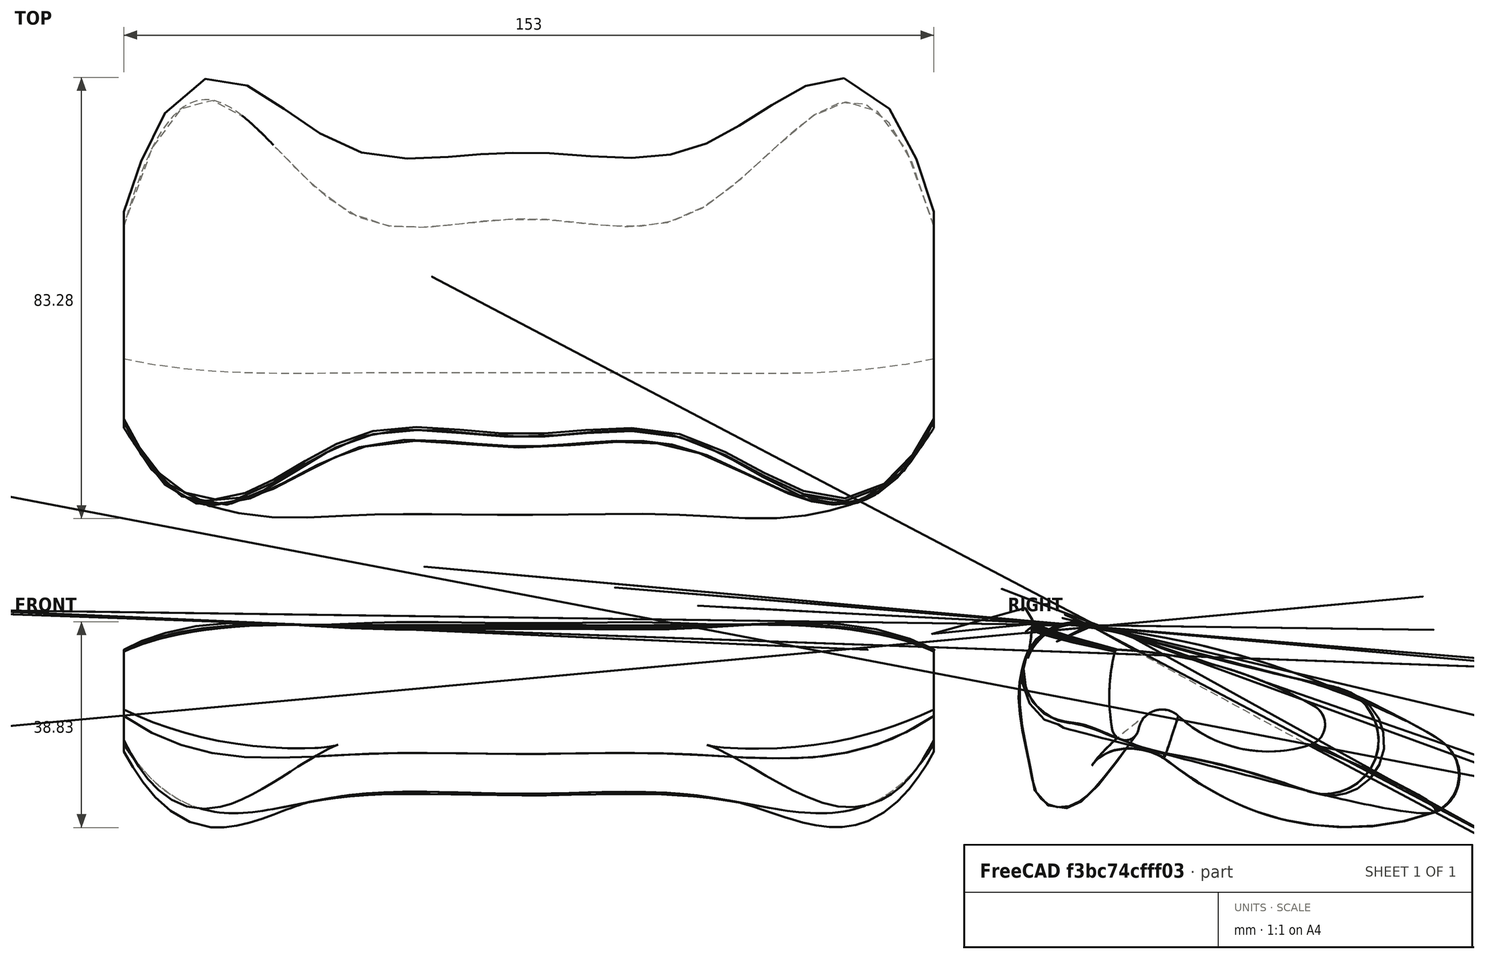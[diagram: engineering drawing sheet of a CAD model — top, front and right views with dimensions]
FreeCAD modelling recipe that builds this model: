
FCSTD DOCUMENT  (FreeCAD 0.20R29410 (Git))
Label: manette
License: All rights reserved
LicenseURL: http://en.wikipedia.org/wiki/All_rights_reserved
objects: Part::FeaturePython×9, Sketcher::SketchObject×7, Part::Face×2
note: 18 computed .brp shape members not serialized (recipe doc carries the construction recipe); baked Part::Feature solids carry a one-line shape summary decoded from their .brp

FEATURE [Sketcher::SketchObject] Sketch001
  FullyConstrained = true
  Placement = pos=(0,0,0) rot=(0.57735,0.57735,0.57735;2.0944rad)
  sketch-geometry (7):
    g0: ArcOfCircle CenterX=51.2288 CenterY=20.8676 CenterZ=0 NormalX=0 NormalY=0 NormalZ=1 AngleXU=0 Radius=4 StartAngle=5.03579 EndAngle=7.33836
    g1: ArcOfCircle CenterX=44.5551 CenterY=40.779 CenterZ=0 NormalX=0 NormalY=0 NormalZ=1 AngleXU=0 Radius=25 StartAngle=3.96161 EndAngle=5.03579
    g2: ArcOfCircle CenterX=24.4301 CenterY=19.2098 CenterZ=0 NormalX=0 NormalY=0 NormalZ=1 AngleXU=0 Radius=4.5 StartAngle=0.820021 EndAngle=2.96507
    g3: ArcOfCircle CenterX=17.5 CenterY=20.4459 CenterZ=0 NormalX=0 NormalY=0 NormalZ=1 AngleXU=0 Radius=2.53946 StartAngle=3.31811 EndAngle=6.10667
    g4: ArcOfCircle CenterX=49.2692 CenterY=26.1128 CenterZ=0 NormalX=0 NormalY=0 NormalZ=1 AngleXU=0 Radius=34.8101 StartAngle=2.89464 EndAngle=3.31811
    g5: ArcOfCircle CenterX=12.5223 CenterY=-47.4262 CenterZ=0 NormalX=0 NormalY=0 NormalZ=1 AngleXU=0 Radius=82.5 StartAngle=1.05517 EndAngle=1.52837
    g6: ArcOfCircle CenterX=16 CenterY=34.5 CenterZ=0 NormalX=0 NormalY=0 NormalZ=1 AngleXU=0 Radius=0.5 StartAngle=1.52837 EndAngle=2.89464
  constraints (21):
    c: Tangent(g2,g3) = 1.5708
    c: Tangent(g2,g1) = 1.5708
    c: Tangent(g1,g0) = -1.5708
    c: Tangent(g3,g4) = -1.5708
    c: Tangent(g0,g5) = -1.5708
    c: DistanceX(g1,g0) = 25
    c: DistanceX(g2,g1) = 7.5
    c: DistanceY(g3,g2) = 0
    c: DistanceX(g3,g2) = 5
    c: DistanceX(g-1,g3) = 15
    c: DistanceY(g-1,g3) = 20
    c: Radius(g1) = 25
    c: Radius(g2) = 4.5
    c: Radius(g0) = 4
    c: Radius(g5) = 82.5
    c: Tangent(g5,g6) = -1.5708
    c: Tangent(g4,g6) = -1.5708
    c: Radius(g6) = 0.5
    c: DistanceX(g3,g6) = 1
    c: DistanceY(g3,g6) = 14.5
    c: DistanceY(g-1,g1) = 22.5
FEATURE [Sketcher::SketchObject] Sketch002
  FullyConstrained = true
  Placement = pos=(20,0,0) rot=(0.57735,0.57735,0.57735;2.0944rad)
  sketch-geometry (7):
    g0: ArcOfCircle CenterX=72.5307 CenterY=11.5172 CenterZ=0 NormalX=0 NormalY=0 NormalZ=1 AngleXU=0 Radius=7.77 StartAngle=5.03579 EndAngle=7.33312
    g1: ArcOfCircle CenterX=59.1103 CenterY=51.558 CenterZ=0 NormalX=0 NormalY=0 NormalZ=1 AngleXU=0 Radius=50 StartAngle=3.96161 EndAngle=5.03579
    g2: ArcOfCircle CenterX=18.8601 CenterY=8.41956 CenterZ=0 NormalX=0 NormalY=0 NormalZ=1 AngleXU=0 Radius=9 StartAngle=0.820021 EndAngle=2.96507
    g3: ArcOfCircle CenterX=5 CenterY=10.8919 CenterZ=0 NormalX=0 NormalY=0 NormalZ=1 AngleXU=0 Radius=5.07892 StartAngle=3.31811 EndAngle=6.10667
    g4: ArcOfCircle CenterX=81.5376 CenterY=24.5444 CenterZ=0 NormalX=0 NormalY=0 NormalZ=1 AngleXU=0 Radius=82.8246 StartAngle=2.96399 EndAngle=3.31811
    g5: ArcOfCircle CenterX=-5.71127 CenterY=-124.863 CenterZ=0 NormalX=0 NormalY=0 NormalZ=1 AngleXU=0 Radius=165 StartAngle=1.04993 EndAngle=1.52986
    g6: ArcOfCircle CenterX=1 CenterY=39 CenterZ=0 NormalX=0 NormalY=0 NormalZ=1 AngleXU=0 Radius=1 StartAngle=1.52986 EndAngle=2.96399
  constraints (21):
    c: Tangent(g2,g3) = 1.5708
    c: Tangent(g2,g1) = 1.5708
    c: Tangent(g1,g0) = -1.5708
    c: Tangent(g3,g4) = -1.5708
    c: DistanceY(g1) = 15
    c: Tangent(g0,g5) = -1.5708
    c: DistanceX(g1,g0) = 50
    c: DistanceX(g2,g1) = 15
    c: DistanceY(g3,g2) = 0
    c: DistanceX(g3,g2) = 10
    c: DistanceX(g-1,g3) = 0
    c: DistanceY(g-1,g3) = 10
    c: Radius(g1) = 50
    c: Radius(g2) = 9
    c: Radius(g0) = 7.77
    c: Radius(g5) = 165
    c: Tangent(g5,g6) = -1.5708
    c: Tangent(g4,g6) = -1.5708
    c: Radius(g6) = 1
    c: DistanceX(g3,g6) = 1
    c: DistanceY(g3,g6) = 29
FEATURE [Sketcher::SketchObject] Sketch  label="Sketch003"
  FullyConstrained = true
  Placement = pos=(45,0,0) rot=(0.57735,0.57735,0.57735;2.0944rad)
  sketch-geometry (7):
    g0: ArcOfCircle CenterX=56.4123 CenterY=17.5 CenterZ=0 NormalX=0 NormalY=0 NormalZ=1 AngleXU=0 Radius=10 StartAngle=4.45971 EndAngle=7.6013
    g1: LineSegment StartX=13.246 StartY=18.3175 StartZ=0 EndX=24.8649 EndY=15.3175 EndZ=0
    g2: LineSegment StartX=24.8649 StartY=15.3175 StartZ=0 EndX=53.9123 EndY=7.81754 EndZ=0
    g3: ArcOfCircle CenterX=8 CenterY=30 CenterZ=0 NormalX=0 NormalY=0 NormalZ=1 AngleXU=0 Radius=10 StartAngle=1.31812 EndAngle=4.45971
    g4: LineSegment StartX=5.5 StartY=20.3175 StartZ=0 EndX=13.246 EndY=18.3175 EndZ=0
    g5: LineSegment StartX=58.9123 StartY=27.1825 StartZ=0 EndX=13.4047 EndY=38.9325 EndZ=0
    g6: LineSegment StartX=13.4047 StartY=38.9325 StartZ=0 EndX=10.5 EndY=39.6825 EndZ=0
  constraints (17):
    c: Tangent(g2,g0) = -1.5708
    c: Tangent(g0,g5) = -1.5708
    c: DistanceY(g-1,g0) = 17.5
    c: Distance(g3,g2) = 50
    c: Distance(g1) = 12
    c: Radius(g0) = 10
    c: Equal(g3,g0)
    c: Tangent(g4,g1) = -1.5708
    c: Tangent(g1,g2) = -1.5708
    c: Tangent(g4,g3) = -1.5708
    c: Tangent(g3,g6) = -1.5708
    c: DistanceX(g-1,g3) = 8
    c: DistanceY(g-1,g3) = 30
    c: Coincident(g5,g6)
    c: Tangent(g5,g6,g5) = -1.5708
    c: Distance(g6) = 3
    c: Distance(g4) = 8
FEATURE [Sketcher::SketchObject] Sketch003  label="Sketch005"
  FullyConstrained = true
  Placement = pos=(105,0,0) rot=(0.57735,0.57735,0.57735;2.0944rad)
  sketch-geometry (7):
    g0: ArcOfCircle CenterX=56.4123 CenterY=17.5 CenterZ=0 NormalX=0 NormalY=0 NormalZ=1 AngleXU=0 Radius=10 StartAngle=4.45971 EndAngle=7.6013
    g1: LineSegment StartX=5.5 StartY=20.3175 StartZ=0 EndX=13.246 EndY=18.3175 EndZ=0
    g2: LineSegment StartX=13.246 StartY=18.3175 StartZ=0 EndX=24.8649 EndY=15.3175 EndZ=0
    g3: LineSegment StartX=24.8649 StartY=15.3175 StartZ=0 EndX=53.9123 EndY=7.81754 EndZ=0
    g4: ArcOfCircle CenterX=8 CenterY=30 CenterZ=0 NormalX=0 NormalY=0 NormalZ=1 AngleXU=0 Radius=10 StartAngle=1.31812 EndAngle=4.45971
    g5: LineSegment StartX=58.9123 StartY=27.1825 StartZ=0 EndX=13.4047 EndY=38.9325 EndZ=0
    g6: LineSegment StartX=13.4047 StartY=38.9325 StartZ=0 EndX=10.5 EndY=39.6825 EndZ=0
  constraints (16):
    c: Tangent(g3,g0) = -1.5708
    c: Tangent(g0,g5) = -1.5708
    c: DistanceY(g-1,g0) = 17.5
    c: Distance(g1,g3) = 50
    c: Distance(g1) = 8
    c: Distance(g2) = 12
    c: Radius(g0) = 10
    c: DistanceY(g-1,g4) = 30
    c: Tangent(g1,g2) = -1.5708
    c: Tangent(g2,g3) = -1.5708
    c: Tangent(g4,g1) = -1.5708
    c: Tangent(g4,g6) = -1.5708
    c: DistanceX(g-1,g4) = 8
    c: Parallel(g5,g3)
    c: Tangent(g5,g6) = -1.5708
    c: Distance(g6) = 3
FEATURE [Sketcher::SketchObject] Sketch004  label="Sketch006"
  FullyConstrained = true
  Placement = pos=(133,0,0) rot=(0.57735,0.57735,0.57735;2.0944rad)
  sketch-geometry (7):
    g0: ArcOfCircle CenterX=72.5307 CenterY=11.5172 CenterZ=0 NormalX=0 NormalY=0 NormalZ=1 AngleXU=0 Radius=7.77 StartAngle=5.03579 EndAngle=7.33312
    g1: ArcOfCircle CenterX=59.1103 CenterY=51.558 CenterZ=0 NormalX=0 NormalY=0 NormalZ=1 AngleXU=0 Radius=50 StartAngle=3.96161 EndAngle=5.03579
    g2: ArcOfCircle CenterX=18.8601 CenterY=8.41956 CenterZ=0 NormalX=0 NormalY=0 NormalZ=1 AngleXU=0 Radius=9 StartAngle=0.820021 EndAngle=2.96507
    g3: ArcOfCircle CenterX=5 CenterY=10.8919 CenterZ=0 NormalX=0 NormalY=0 NormalZ=1 AngleXU=0 Radius=5.07892 StartAngle=3.31811 EndAngle=6.10667
    g4: ArcOfCircle CenterX=81.5376 CenterY=24.5444 CenterZ=0 NormalX=0 NormalY=0 NormalZ=1 AngleXU=0 Radius=82.8246 StartAngle=2.96399 EndAngle=3.31811
    g5: ArcOfCircle CenterX=-5.71127 CenterY=-124.863 CenterZ=0 NormalX=0 NormalY=0 NormalZ=1 AngleXU=0 Radius=165 StartAngle=1.04993 EndAngle=1.52986
    g6: ArcOfCircle CenterX=1 CenterY=39 CenterZ=0 NormalX=0 NormalY=0 NormalZ=1 AngleXU=0 Radius=1 StartAngle=1.52986 EndAngle=2.96399
  constraints (21):
    c: Tangent(g2,g3) = 1.5708
    c: Tangent(g2,g1) = 1.5708
    c: Tangent(g1,g0) = -1.5708
    c: Tangent(g3,g4) = -1.5708
    c: DistanceY(g1) = 15
    c: Tangent(g0,g5) = -1.5708
    c: DistanceX(g1,g0) = 50
    c: DistanceX(g2,g1) = 15
    c: DistanceY(g3,g2) = 0
    c: DistanceX(g3,g2) = 10
    c: DistanceX(g-1,g3) = 0
    c: DistanceY(g-1,g3) = 10
    c: Radius(g1) = 50
    c: Radius(g2) = 9
    c: Radius(g0) = 7.77
    c: Radius(g5) = 165
    c: Tangent(g5,g6) = -1.5708
    c: Tangent(g4,g6) = -1.5708
    c: Radius(g6) = 1
    c: DistanceX(g3,g6) = 1
    c: DistanceY(g3,g6) = 29
FEATURE [Sketcher::SketchObject] Sketch005  label="Sketch007"
  FullyConstrained = true
  Placement = pos=(153,0,0) rot=(0.57735,0.57735,0.57735;2.0944rad)
  sketch-geometry (7):
    g0: ArcOfCircle CenterX=51.2288 CenterY=20.8676 CenterZ=0 NormalX=0 NormalY=0 NormalZ=1 AngleXU=0 Radius=4 StartAngle=5.03579 EndAngle=7.33836
    g1: ArcOfCircle CenterX=44.5551 CenterY=40.779 CenterZ=0 NormalX=0 NormalY=0 NormalZ=1 AngleXU=0 Radius=25 StartAngle=3.96161 EndAngle=5.03579
    g2: ArcOfCircle CenterX=24.4301 CenterY=19.2098 CenterZ=0 NormalX=0 NormalY=0 NormalZ=1 AngleXU=0 Radius=4.5 StartAngle=0.820021 EndAngle=2.96507
    g3: ArcOfCircle CenterX=17.5 CenterY=20.4459 CenterZ=0 NormalX=0 NormalY=0 NormalZ=1 AngleXU=0 Radius=2.53946 StartAngle=3.31811 EndAngle=6.10667
    g4: ArcOfCircle CenterX=49.2692 CenterY=26.1128 CenterZ=0 NormalX=0 NormalY=0 NormalZ=1 AngleXU=0 Radius=34.8101 StartAngle=2.89464 EndAngle=3.31811
    g5: ArcOfCircle CenterX=12.5223 CenterY=-47.4262 CenterZ=0 NormalX=0 NormalY=0 NormalZ=1 AngleXU=0 Radius=82.5 StartAngle=1.05517 EndAngle=1.52837
    g6: ArcOfCircle CenterX=16 CenterY=34.5 CenterZ=0 NormalX=0 NormalY=0 NormalZ=1 AngleXU=0 Radius=0.5 StartAngle=1.52837 EndAngle=2.89464
  constraints (21):
    c: Tangent(g2,g3) = 1.5708
    c: Tangent(g2,g1) = 1.5708
    c: Tangent(g1,g0) = -1.5708
    c: Tangent(g3,g4) = -1.5708
    c: Tangent(g0,g5) = -1.5708
    c: DistanceX(g1,g0) = 25
    c: DistanceX(g2,g1) = 7.5
    c: DistanceY(g3,g2) = 0
    c: DistanceX(g3,g2) = 5
    c: DistanceX(g-1,g3) = 15
    c: DistanceY(g-1,g3) = 20
    c: Radius(g1) = 25
    c: Radius(g2) = 4.5
    c: Radius(g0) = 4
    c: Radius(g5) = 82.5
    c: Tangent(g5,g6) = -1.5708
    c: Tangent(g4,g6) = -1.5708
    c: Radius(g6) = 0.5
    c: DistanceX(g3,g6) = 1
    c: DistanceY(g3,g6) = 14.5
    c: DistanceY(g-1,g1) = 22.5
FEATURE [Sketcher::SketchObject] Sketch006  label="Sketch004"
  FullyConstrained = true
  Placement = pos=(75,0,0) rot=(0.57735,0.57735,0.57735;2.0944rad)
  sketch-geometry (7):
    g0: ArcOfCircle CenterX=56.4123 CenterY=17.5 CenterZ=0 NormalX=0 NormalY=0 NormalZ=1 AngleXU=0 Radius=10 StartAngle=4.45971 EndAngle=7.6013
    g1: LineSegment StartX=13.246 StartY=18.3175 StartZ=0 EndX=24.8649 EndY=15.3175 EndZ=0
    g2: LineSegment StartX=24.8649 StartY=15.3175 StartZ=0 EndX=53.9123 EndY=7.81754 EndZ=0
    g3: ArcOfCircle CenterX=8 CenterY=30 CenterZ=0 NormalX=0 NormalY=0 NormalZ=1 AngleXU=0 Radius=10 StartAngle=1.31812 EndAngle=4.45971
    g4: LineSegment StartX=5.5 StartY=20.3175 StartZ=0 EndX=13.246 EndY=18.3175 EndZ=0
    g5: LineSegment StartX=58.9123 StartY=27.1825 StartZ=0 EndX=13.4047 EndY=38.9325 EndZ=0
    g6: LineSegment StartX=13.4047 StartY=38.9325 StartZ=0 EndX=10.5 EndY=39.6825 EndZ=0
  constraints (17):
    c: Tangent(g2,g0) = -1.5708
    c: Tangent(g0,g5) = -1.5708
    c: DistanceY(g-1,g0) = 17.5
    c: Distance(g3,g2) = 50
    c: Distance(g1) = 12
    c: Radius(g0) = 10
    c: Equal(g3,g0)
    c: Tangent(g4,g1) = -1.5708
    c: Tangent(g1,g2) = -1.5708
    c: Tangent(g4,g3) = -1.5708
    c: Tangent(g3,g6) = -1.5708
    c: DistanceX(g-1,g3) = 8
    c: DistanceY(g-1,g3) = 30
    c: Coincident(g5,g6)
    c: Tangent(g5,g6,g5) = -1.5708
    c: Distance(g6) = 3
    c: Distance(g4) = 8
FEATURE [Part::FeaturePython] Interpolation_Curve  # WARN: FeaturePython — macro-defined, semantics opaque (R4)
  CustomTangents = false
  DetectAligned = false
  Parameters = [0,0.150341,0.315001,0.491988,0.668974,0.849659,1]
  Parametrization = 0
  Periodic = false
  PointList = -> [Sketch001,Sketch002,Sketch,Sketch006,Sketch003,Sketch004,Sketch005]
  Polygonal = false
  Tangents = (7) [(0.420603,-0.878702,0.22578),(0.97648,0.212022,0.0391605),(0.953715,0.298244,-0.0384563),(0.999967,-0.00806821,0.00063064),+3 more]
  Tolerance = 1e-07
  UTurns = 0
  VTurns = 0
  WireOutput = false
FEATURE [Part::FeaturePython] Interpolation_Curve001  # WARN: FeaturePython — macro-defined, semantics opaque (R4)
  CustomTangents = false
  DetectAligned = false
  Parameters = [0,0.152636,0.313613,0.491722,0.669831,0.847364,1]
  Parametrization = 0
  Periodic = false
  PointList = -> [Sketch001,Sketch002,Sketch,Sketch006,Sketch003,Sketch004,Sketch005]
  Polygonal = false
  Tangents = (7) [(0.408413,-0.895345,0.177641),(0.983736,0.157982,0.0854665),(0.963517,0.267605,-0.00475513),(0.999972,-0.00742088,-0.000463863),+3 more]
  Tolerance = 1e-07
  UTurns = 0
  VTurns = 0
  WireOutput = false
FEATURE [Part::FeaturePython] Interpolation_Curve002  # WARN: FeaturePython — macro-defined, semantics opaque (R4)
  CustomTangents = false
  DetectAligned = false
  Parameters = [0,0.156734,0.317385,0.492013,0.666641,0.843266,1]
  Parametrization = 0
  Periodic = false
  PointList = -> [Sketch001,Sketch002,Sketch,Sketch006,Sketch003,Sketch004,Sketch005]
  Polygonal = false
  Tangents = (7) [(0.362068,-0.698177,-0.617621),(0.969293,-0.00285222,0.245893),(0.958935,0.156031,0.23685),(0.99997,-0.00353331,-0.00696508),+3 more]
  Tolerance = 1e-07
  UTurns = 0
  VTurns = 0
  WireOutput = false
FEATURE [Part::FeaturePython] Interpolation_Curve003  # WARN: FeaturePython — macro-defined, semantics opaque (R4)
  CustomTangents = false
  DetectAligned = false
  Parameters = [0,0.148521,0.309482,0.491382,0.673283,0.851479,1]
  Parametrization = 0
  Periodic = false
  PointList = -> [Sketch001,Sketch002,Sketch,Sketch006,Sketch003,Sketch004,Sketch005]
  Polygonal = false
  Tangents = (7) [(0.474797,-0.553753,-0.684051),(0.988732,-0.0370949,0.14503),(0.971114,0.105575,0.21399),(0.999977,-0.00235665,-0.00637812),+3 more]
  Tolerance = 1e-07
  UTurns = 0
  VTurns = 0
  WireOutput = false
FEATURE [Part::FeaturePython] Interpolation_Curve004  # WARN: FeaturePython — macro-defined, semantics opaque (R4)
  CustomTangents = false
  DetectAligned = false
  Parameters = [0,0.137844,0.317326,0.509614,0.701901,0.862156,1]
  Parametrization = 0
  Periodic = false
  PointList = -> [Sketch005,Sketch004,Sketch003,Sketch006,Sketch,Sketch002,Sketch001]
  Polygonal = false
  Tangents = (7) [(-0.810963,-0.178339,-0.557257),(-0.990434,-0.0498443,-0.128669),(-0.999116,0.00888395,0.0410823),(-1,-0.000199676,0.000103465),+3 more]
  Tolerance = 1e-07
  UTurns = 0
  VTurns = 0
  WireOutput = false
FEATURE [Part::FeaturePython] Interpolation_Curve005  # WARN: FeaturePython — macro-defined, semantics opaque (R4)
  CustomTangents = false
  DetectAligned = false
  Parameters = [0,0.169154,0.339081,0.493977,0.648874,0.830846,1]
  Parametrization = 0
  Periodic = false
  PointList = -> [Sketch001,Sketch002,Sketch,Sketch006,Sketch003,Sketch004,Sketch005]
  Polygonal = false
  Tangents = (7) [(0.250432,0.891614,-0.377237),(0.866386,-0.498768,-0.0246198),(0.920988,-0.379794,0.0868206),(0.999968,0.00793356,-0.00129816),+3 more]
  Tolerance = 1e-07
  UTurns = 0
  VTurns = 0
  WireOutput = false
FEATURE [Part::FeaturePython] Interpolation_Curve006  # WARN: FeaturePython — macro-defined, semantics opaque (R4)
  CustomTangents = false
  DetectAligned = false
  Parameters = [0,0.165718,0.34719,0.506394,0.665597,0.834282,1]
  Parametrization = 0
  Periodic = false
  PointList = -> [Sketch005,Sketch004,Sketch003,Sketch006,Sketch,Sketch002,Sketch001]
  Polygonal = false
  Tangents = (7) [(-0.26491,0.913609,-0.308448),(-0.935614,-0.276116,0.219969),(-0.939498,-0.310735,0.144177),(-0.999966,-0.0073485,0.00381124),+3 more]
  Tolerance = 1e-07
  UTurns = 0
  VTurns = 0
  WireOutput = false
FEATURE [Part::FeaturePython] Gordon  # WARN: FeaturePython — macro-defined, semantics opaque (R4)
  FlipNormal = false
  MaxCtrlPts = 80
  Output = 0
  SamplesU = 16
  SamplesV = 16
  Sources = -> [Sketch001,Sketch002,Sketch,Sketch003,Sketch004,Sketch005,Sketch006,Interpolation_Curve,Interpolation_Curve001,Interpolation_Curve002,Interpolation_Curve003,Interpolation_Curve004,Interpolation_Curve005,Interpolation_Curve006]
  Tol2D = 1e-05
  Tol3D = 0.01
FEATURE [Part::FeaturePython] Gordon001  # WARN: FeaturePython — macro-defined, semantics opaque (R4)
  FlipNormal = false
  MaxCtrlPts = 80
  Output = 0
  SamplesU = 16
  SamplesV = 16
  Sources = -> [Sketch005,Sketch006,Sketch001,Sketch,Sketch002,Sketch003,Sketch004,Interpolation_Curve004,Interpolation_Curve005]
  Tol2D = 1e-05
  Tol3D = 0.01
FEATURE [Part::Face] Face
  FaceMakerClass = Part::FaceMakerBullseye
  Sources = -> [Sketch001]
FEATURE [Part::Face] Face001
  FaceMakerClass = Part::FaceMakerBullseye
  Sources = -> [Sketch005]
